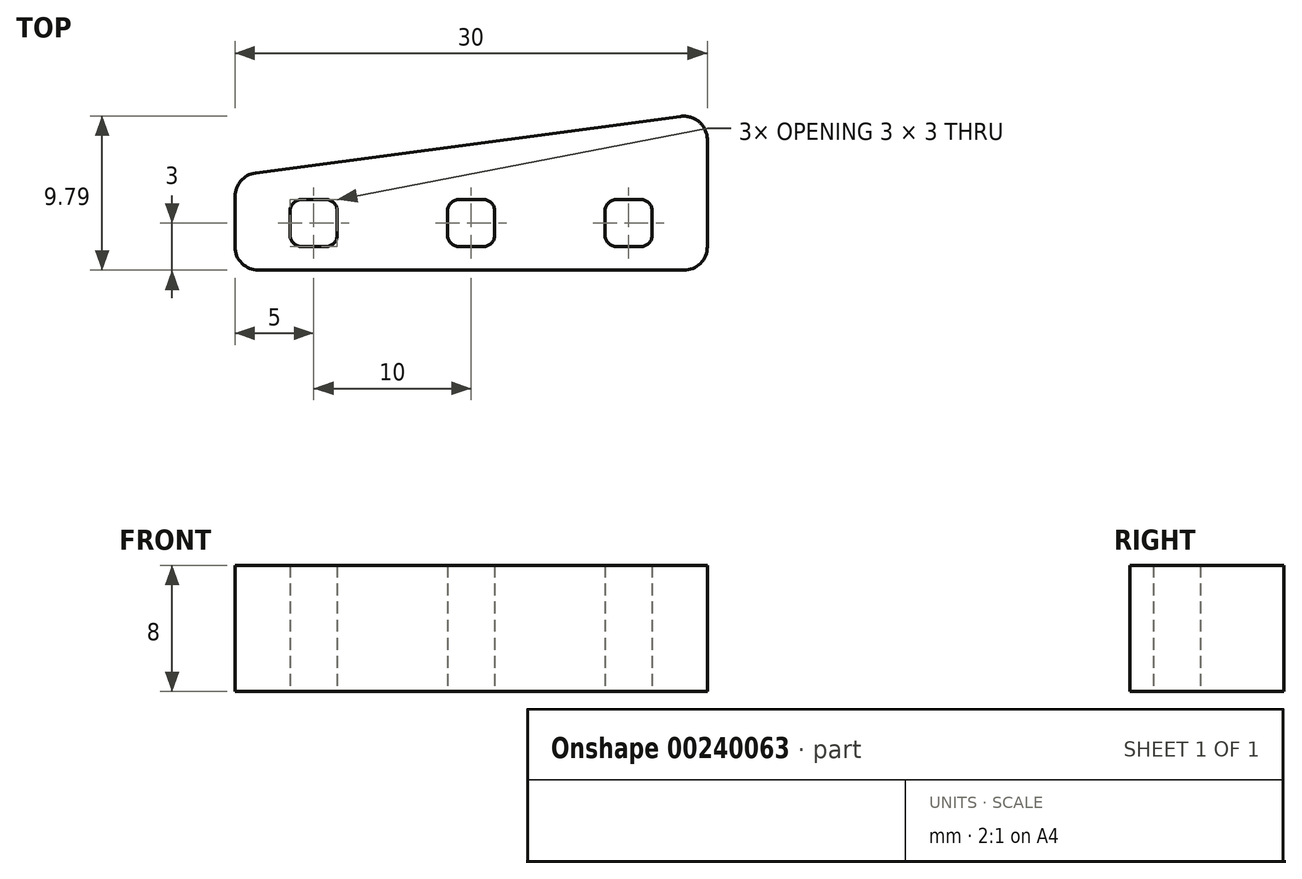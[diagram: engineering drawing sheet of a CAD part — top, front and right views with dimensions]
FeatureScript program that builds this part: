
annotation { "Feature Type Name" : "Feature", "Feature Type Description" : "" }
export const myFeature = defineFeature(function(context is Context, id is Id, definition is map)
    precondition{}
    {
        {
            var Q0;
            Q0=qCreatedBy(makeId("Top.planeOp"),FACE);
            var sketch = newSketch(context, id + "F0", { "sketchPlane" : qUnion([Q0])});
            skLineSegment(sketch, "E0", {"start": v(0, 0) * mm, "end": v(30, 0) * mm});
            skLineSegment(sketch, "E1", {"start": v(0, 0) * mm, "end": v(0, 6) * mm});
            skLineSegment(sketch, "E2", {"start": v(30, 0) * mm, "end": v(30, 10) * mm});
            skLineSegment(sketch, "E3", {"start": v(30, 10) * mm, "end": v(0, 6) * mm});
            skSolve(sketch);
        }
        {
            var Q0;
            Q0 = qSketchRegion(id + "F0", true);
            extrude(context, id + "F1", {"entities" : qUnion([Q0]), "depth" : 8 * mm});
        }
        {
            var Q0;
            Q0=makeQuery(id+"F1.opExtrude","SWEPT_EDGE",EDGE,{"disambiguationData":[OSD([sQuery(id+"F0.wireOp",EDGE,"E0"),sQuery(id+"F0.wireOp",EDGE,"E2")])]});
            var Q1;
            Q1=makeQuery(id+"F1.opExtrude","SWEPT_EDGE",EDGE,{"disambiguationData":[OSD([sQuery(id+"F0.wireOp",EDGE,"E0"),sQuery(id+"F0.wireOp",EDGE,"E1")])]});
            var Q2;
            Q2=makeQuery(id+"F1.opExtrude","SWEPT_EDGE",EDGE,{"disambiguationData":[OSD([sQuery(id+"F0.wireOp",EDGE,"E2"),sQuery(id+"F0.wireOp",EDGE,"E3")])]});
            var Q3;
            Q3=makeQuery(id+"F1.opExtrude","SWEPT_EDGE",EDGE,{"disambiguationData":[OSD([sQuery(id+"F0.wireOp",EDGE,"E1"),sQuery(id+"F0.wireOp",EDGE,"E3")])]});
            fillet(context, id + "F2", {"entities" : qUnion([Q0, Q1, Q2, Q3]), "radius" : 1.5 * mm, "tangentPropagation" : true, "allowEdgeOverflow" : false});
        }
        {
            var Q0;
            Q0=qCreatedBy(makeId("Top.planeOp"),FACE);
            var sketch = newSketch(context, id + "F3", { "sketchPlane" : qUnion([Q0])});
            skLineSegment(sketch, "E4.bottom", {"start": v(1.5, -1.5) * mm, "end": v(-1.5, -1.5) * mm});
            skLineSegment(sketch, "E4.top", {"start": v(1.5, 1.5) * mm, "end": v(-1.5, 1.5) * mm});
            skLineSegment(sketch, "E4.left", {"start": v(1.5, -1.5) * mm, "end": v(1.5, 1.5) * mm});
            skLineSegment(sketch, "E4.right", {"start": v(-1.5, -1.5) * mm, "end": v(-1.5, 1.5) * mm});
            skPoint(sketch, "E4.middle", {"position": v(0, 0) * mm});
            skSolve(sketch);
        }
        {
            var Q0;
            Q0 = qSketchRegion(id + "F3", true);
            extrude(context, id + "F4", {"entities" : qUnion([Q0]), "depth" : 9 * mm});
        }
        {
            var Q0;
            Q0=makeQuery(id+"F4.opExtrude","SWEPT_EDGE",EDGE,{"disambiguationData":[OSD([sQuery(id+"F3.wireOp",EDGE,"E4.bottom"),sQuery(id+"F3.wireOp",EDGE,"E4.left")])]});
            var Q1;
            Q1=makeQuery(id+"F4.opExtrude","SWEPT_EDGE",EDGE,{"disambiguationData":[OSD([sQuery(id+"F3.wireOp",EDGE,"E4.bottom"),sQuery(id+"F3.wireOp",EDGE,"E4.right")])]});
            var Q2;
            Q2=makeQuery(id+"F4.opExtrude","SWEPT_EDGE",EDGE,{"disambiguationData":[OSD([sQuery(id+"F3.wireOp",EDGE,"E4.top"),sQuery(id+"F3.wireOp",EDGE,"E4.left")])]});
            var Q3;
            Q3=makeQuery(id+"F4.opExtrude","SWEPT_EDGE",EDGE,{"disambiguationData":[OSD([sQuery(id+"F3.wireOp",EDGE,"E4.top"),sQuery(id+"F3.wireOp",EDGE,"E4.right")])]});
            fillet(context, id + "F5", {"entities" : qUnion([Q0, Q1, Q2, Q3]), "radius" : 0.75 * mm, "tangentPropagation" : true, "allowEdgeOverflow" : false});
        }
        {
            var Q0;
            Q0=makeQuery(id+"F4.opExtrude","SWEPT_BODY",BODY,{"disambiguationData":[OSD([sQuery(id+"F3.wireOp",EDGE,"E4.bottom"),sQuery(id+"F3.wireOp",EDGE,"E4.top"),sQuery(id+"F3.wireOp",EDGE,"E4.left"),sQuery(id+"F3.wireOp",EDGE,"E4.right")])]});
            transform(context, id + "F6", {"entities" : qUnion([Q0]), "transformType" : TransformType.TRANSLATION_3D, "dx" : 25 * mm, "dy" : 4 * mm, "dz" : 0 * mm, "makeCopy" : false});
        }
        {
            var Q0;
            Q0=makeQuery(id+"F4.opExtrude","SWEPT_BODY",BODY,{"disambiguationData":[OSD([sQuery(id+"F3.wireOp",EDGE,"E4.bottom"),sQuery(id+"F3.wireOp",EDGE,"E4.top"),sQuery(id+"F3.wireOp",EDGE,"E4.left"),sQuery(id+"F3.wireOp",EDGE,"E4.right")])]});
            transform(context, id + "F7", {"entities" : qUnion([Q0]), "transformType" : TransformType.COPY});
        }
        {
            var Q0;
            Q0=makeQuery(id+"F7.opPattern","COPY",BODY,{"derivedFrom":makeQuery(id+"F4.opExtrude","SWEPT_BODY",BODY,{"disambiguationData":[OSD([sQuery(id+"F3.wireOp",EDGE,"E4.bottom"),sQuery(id+"F3.wireOp",EDGE,"E4.top"),sQuery(id+"F3.wireOp",EDGE,"E4.left"),sQuery(id+"F3.wireOp",EDGE,"E4.right")])]}),"instanceName":"1"});
            transform(context, id + "F8", {"entities" : qUnion([Q0]), "transformType" : TransformType.TRANSLATION_3D, "dx" : -10 * mm, "dy" : 0 * mm, "dz" : 0 * mm, "makeCopy" : false});
        }
        {
            var Q0;
            Q0=makeQuery(id+"F7.opPattern","COPY",BODY,{"derivedFrom":makeQuery(id+"F4.opExtrude","SWEPT_BODY",BODY,{"disambiguationData":[OSD([sQuery(id+"F3.wireOp",EDGE,"E4.bottom"),sQuery(id+"F3.wireOp",EDGE,"E4.top"),sQuery(id+"F3.wireOp",EDGE,"E4.left"),sQuery(id+"F3.wireOp",EDGE,"E4.right")])]}),"instanceName":"1"});
            transform(context, id + "F9", {"entities" : qUnion([Q0]), "transformType" : TransformType.COPY});
        }
        {
            var Q0;
            Q0=makeQuery(id+"F9.opPattern","COPY",BODY,{"derivedFrom":makeQuery(id+"F7.opPattern","COPY",BODY,{"derivedFrom":makeQuery(id+"F4.opExtrude","SWEPT_BODY",BODY,{"disambiguationData":[OSD([sQuery(id+"F3.wireOp",EDGE,"E4.bottom"),sQuery(id+"F3.wireOp",EDGE,"E4.top"),sQuery(id+"F3.wireOp",EDGE,"E4.left"),sQuery(id+"F3.wireOp",EDGE,"E4.right")])]}),"instanceName":"1"}),"instanceName":"1"});
            transform(context, id + "F10", {"entities" : qUnion([Q0]), "transformType" : TransformType.TRANSLATION_3D, "dx" : -10 * mm, "dy" : 0 * mm, "dz" : 0 * mm, "makeCopy" : false});
        }
        {
            var Q0;
            Q0=makeQuery(id+"F4.opExtrude","SWEPT_BODY",BODY,{"disambiguationData":[OSD([sQuery(id+"F3.wireOp",EDGE,"E4.bottom"),sQuery(id+"F3.wireOp",EDGE,"E4.top"),sQuery(id+"F3.wireOp",EDGE,"E4.left"),sQuery(id+"F3.wireOp",EDGE,"E4.right")])]});
            var Q1;
            Q1=makeQuery(id+"F7.opPattern","COPY",BODY,{"derivedFrom":makeQuery(id+"F4.opExtrude","SWEPT_BODY",BODY,{"disambiguationData":[OSD([sQuery(id+"F3.wireOp",EDGE,"E4.bottom"),sQuery(id+"F3.wireOp",EDGE,"E4.top"),sQuery(id+"F3.wireOp",EDGE,"E4.left"),sQuery(id+"F3.wireOp",EDGE,"E4.right")])]}),"instanceName":"1"});
            var Q2;
            Q2=makeQuery(id+"F9.opPattern","COPY",BODY,{"derivedFrom":makeQuery(id+"F7.opPattern","COPY",BODY,{"derivedFrom":makeQuery(id+"F4.opExtrude","SWEPT_BODY",BODY,{"disambiguationData":[OSD([sQuery(id+"F3.wireOp",EDGE,"E4.bottom"),sQuery(id+"F3.wireOp",EDGE,"E4.top"),sQuery(id+"F3.wireOp",EDGE,"E4.left"),sQuery(id+"F3.wireOp",EDGE,"E4.right")])]}),"instanceName":"1"}),"instanceName":"1"});
            transform(context, id + "F11", {"entities" : qUnion([Q0, Q1, Q2]), "transformType" : TransformType.TRANSLATION_3D, "dx" : 0 * mm, "dy" : -1 * mm, "dz" : 0 * mm, "makeCopy" : false});
        }
        {
            var Q0;
            Q0=makeQuery(id+"F7.opPattern","COPY",BODY,{"derivedFrom":makeQuery(id+"F4.opExtrude","SWEPT_BODY",BODY,{"disambiguationData":[OSD([sQuery(id+"F3.wireOp",EDGE,"E4.bottom"),sQuery(id+"F3.wireOp",EDGE,"E4.top"),sQuery(id+"F3.wireOp",EDGE,"E4.left"),sQuery(id+"F3.wireOp",EDGE,"E4.right")])]}),"instanceName":"1"});
            var Q1;
            Q1=makeQuery(id+"F4.opExtrude","SWEPT_BODY",BODY,{"disambiguationData":[OSD([sQuery(id+"F3.wireOp",EDGE,"E4.bottom"),sQuery(id+"F3.wireOp",EDGE,"E4.top"),sQuery(id+"F3.wireOp",EDGE,"E4.left"),sQuery(id+"F3.wireOp",EDGE,"E4.right")])]});
            var Q2;
            Q2=makeQuery(id+"F9.opPattern","COPY",BODY,{"derivedFrom":makeQuery(id+"F7.opPattern","COPY",BODY,{"derivedFrom":makeQuery(id+"F4.opExtrude","SWEPT_BODY",BODY,{"disambiguationData":[OSD([sQuery(id+"F3.wireOp",EDGE,"E4.bottom"),sQuery(id+"F3.wireOp",EDGE,"E4.top"),sQuery(id+"F3.wireOp",EDGE,"E4.left"),sQuery(id+"F3.wireOp",EDGE,"E4.right")])]}),"instanceName":"1"}),"instanceName":"1"});
            var Q3;
            Q3=makeQuery(id+"F1.opExtrude","SWEPT_BODY",BODY,{"disambiguationData":[OSD([sQuery(id+"F0.wireOp",EDGE,"E0"),sQuery(id+"F0.wireOp",EDGE,"E1"),sQuery(id+"F0.wireOp",EDGE,"E2"),sQuery(id+"F0.wireOp",EDGE,"E3")])]});
            booleanBodies(context, id + "F12", {"operationType" : BooleanOperationType.SUBTRACTION, "tools" : qUnion([Q0, Q1, Q2]), "targets" : qUnion([Q3])});
        }
    });
